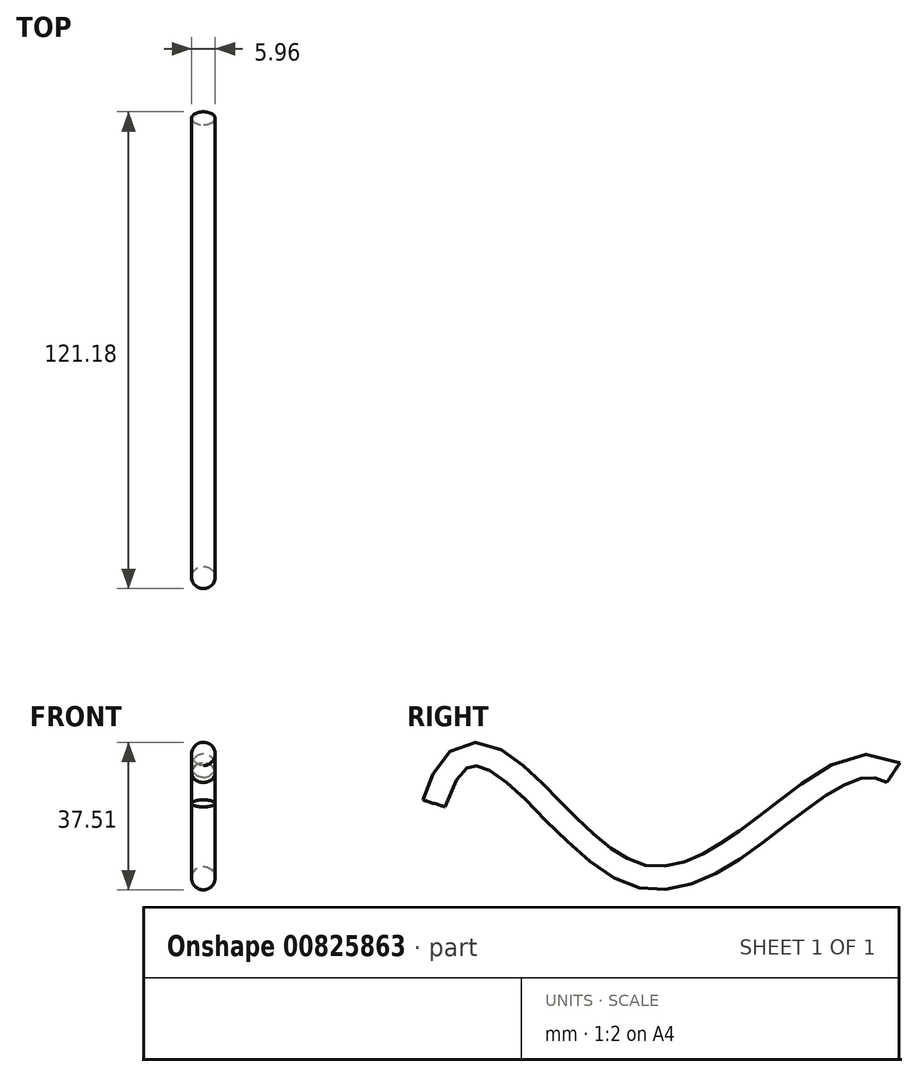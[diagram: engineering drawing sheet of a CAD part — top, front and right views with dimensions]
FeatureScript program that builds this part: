
annotation { "Feature Type Name" : "Feature", "Feature Type Description" : "" }
export const myFeature = defineFeature(function(context is Context, id is Id, definition is map)
    precondition{}
    {
        {
            var Q0;
            Q0=qCreatedBy(makeId("Right.planeOp"),FACE);
            var sketch = newSketch(context, id + "F0", { "sketchPlane" : qUnion([Q0])});
            skFitSpline(sketch, "E0", {"points": [v(62.97, 9.84) * mm, v(-2.07, -16.2) * mm, v(-53.23, 2.22) * mm], "startDerivative": vector(-91.1, 60.84) * mm, "endDerivative": vector(-67.22, -217.24) * mm});
            skSolve(sketch);
        }
        {
            var Q0;
            Q0=sQuery(id+"F0.wireOp",VERTEX,"E0.start");
            var Q1;
            Q1=sQuery(id+"F0.wireOp",EDGE,"E0");
            cPlane(context, id + "F1", {"entities" : qUnion([Q0, Q1]), "cplaneType" : CPlaneType.CURVE_POINT, "offset" : 25.4 * mm, "width" : 152.4 * mm, "height" : 152.4 * mm});
        }
        {
            var Q0;
            Q0=qCreatedBy(id+"F1.planeOp",FACE);
            var sketch = newSketch(context, id + "F2", { "sketchPlane" : qUnion([Q0])});
            skCircle(sketch, "E1", {"center": v(0, 43.47) * mm, "radius": 2.98 * mm});
            skSolve(sketch);
        }
        {
            var Q0;
            Q0=makeQuery(id+"F2.imprint","IMPRINT",FACE,{"disambiguationData":[TD([[makeQuery(id+"F2.imprint","IMPRINT",EDGE,{"derivedFrom":sQuery(id+"F2.wireOp",EDGE,"E1")}),1.0]])]});
            var Q1;
            Q1=sQuery(id+"F0.wireOp",EDGE,"E0");
            sweep(context, id + "F3", {"profiles" : qUnion([Q0]), "path" : qUnion([Q1])});
        }
    });
